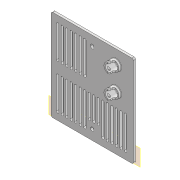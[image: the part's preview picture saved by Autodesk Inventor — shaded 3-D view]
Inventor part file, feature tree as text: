
AUTODESK INVENTOR PART (.ipt)
format: ipt  version: 2020 (Build 240168000, 168)  size: 376,320 bytes
history: native  units: mm
features: other x9, extrude x4, sketch x4, fillet x2
ambient origin geometry x8: Origin, YZ Plane, XZ Plane, XY Plane, X Axis, Y Axis, Z Axis, Center Point
bodies: Body1 (feature_tree)
feature tree (19):
  other  "Sólido1"
  other  "Plano de trabalho1"
  extrude  "Extrusão1"  Depth=0.5mm
  extrude  "Extrusão2"  Depth=0.5mm
  fillet  "Arredondamento1"  Radius=0.5mm
  extrude  "Extrusão3"  Depth=0.5mm
  extrude  "Extrusão4"  Depth=2.0mm
  fillet  "Arredondamento2"  Radius=10.0mm
  sketch  "Esboço1"  dims[d0=0.5mm d1=0.5mm]
  other  "Referência1"
  other  "Referência2"
  sketch  "Esboço2"  dims[d2=1.0mm d3=1.0mm d4=0.5mm]
  sketch  "Esboço3"  dims[d5=0.5mm d6=4.5mm]
  other  "Contorno projetado1"
  other  "Contorno projetado2"
  sketch  "Esboço4"  dims[d7=0.5mm d8=4.5mm d9=10.0mm d10=10.0mm d11=18.0mm d12=23.0mm d13=23.0mm d14=31.0mm d15=42.0mm d16=42.0mm d17=31.0mm d18=31.0mm d19=3.2mm d20=3.2mm d21=70.0mm d23=6.0mm d24=10.0mm d26=10.0mm d28=3.0mm d29=0.0mm d30=3.2mm d31=6.0mm d32=30.0mm d34=6.0mm d35=10.0mm d37=10.0mm d39=3.2mm d40=6.0mm d41=50.0mm d43=6.0mm d44=10.0mm d46=10.0mm d48=20.0mm d50=6.0mm d51=10.0mm d53=10.0mm d55=14.0mm d56=14.0mm d57=3.0mm d58=0.0mm d59=0.5mm d60=6.0mm d61=0.0mm d62=3.0mm d63=100.0mm d64=0.0mm d65=2.0mm]
  other  "Calorímetro.iam"
  other  "suporte_fechamento:2"
  other  "suporte_fechamento:3"
